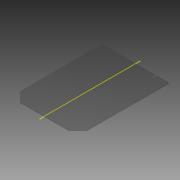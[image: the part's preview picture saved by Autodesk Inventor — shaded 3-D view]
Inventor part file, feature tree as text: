
AUTODESK INVENTOR PART (.ipt)
format: ipt  version: 2015 (Build 190159000, 159)  size: 138,240 bytes
history: native  units: mm
features: reference x7, other x3, extrude x2, fillet x1
ambient origin geometry x8: Origin, YZ Plane, XZ Plane, XY Plane, X Axis, Y Axis, Z Axis, Center Point
bodies: Solid1 (feature_tree)
feature tree (13):
  extrude  "Extrusión1"  Depth=2.0mm TaperAngle=0.0deg
  other  "Desplazar cara1"
  other  "Desplazar cara2"
  other  "Desplazar cara3"
  extrude  "Extrusión2"  Depth=0.2mm
  fillet  "Empalme1"  Radius=0.2mm
  reference  "Referencia2"
  reference  "Referencia3"
  reference  "Referencia4"
  reference  "Referencia5"
  reference  "Referencia6"
  reference  "Referencia7"
  reference  "Referencia8"
